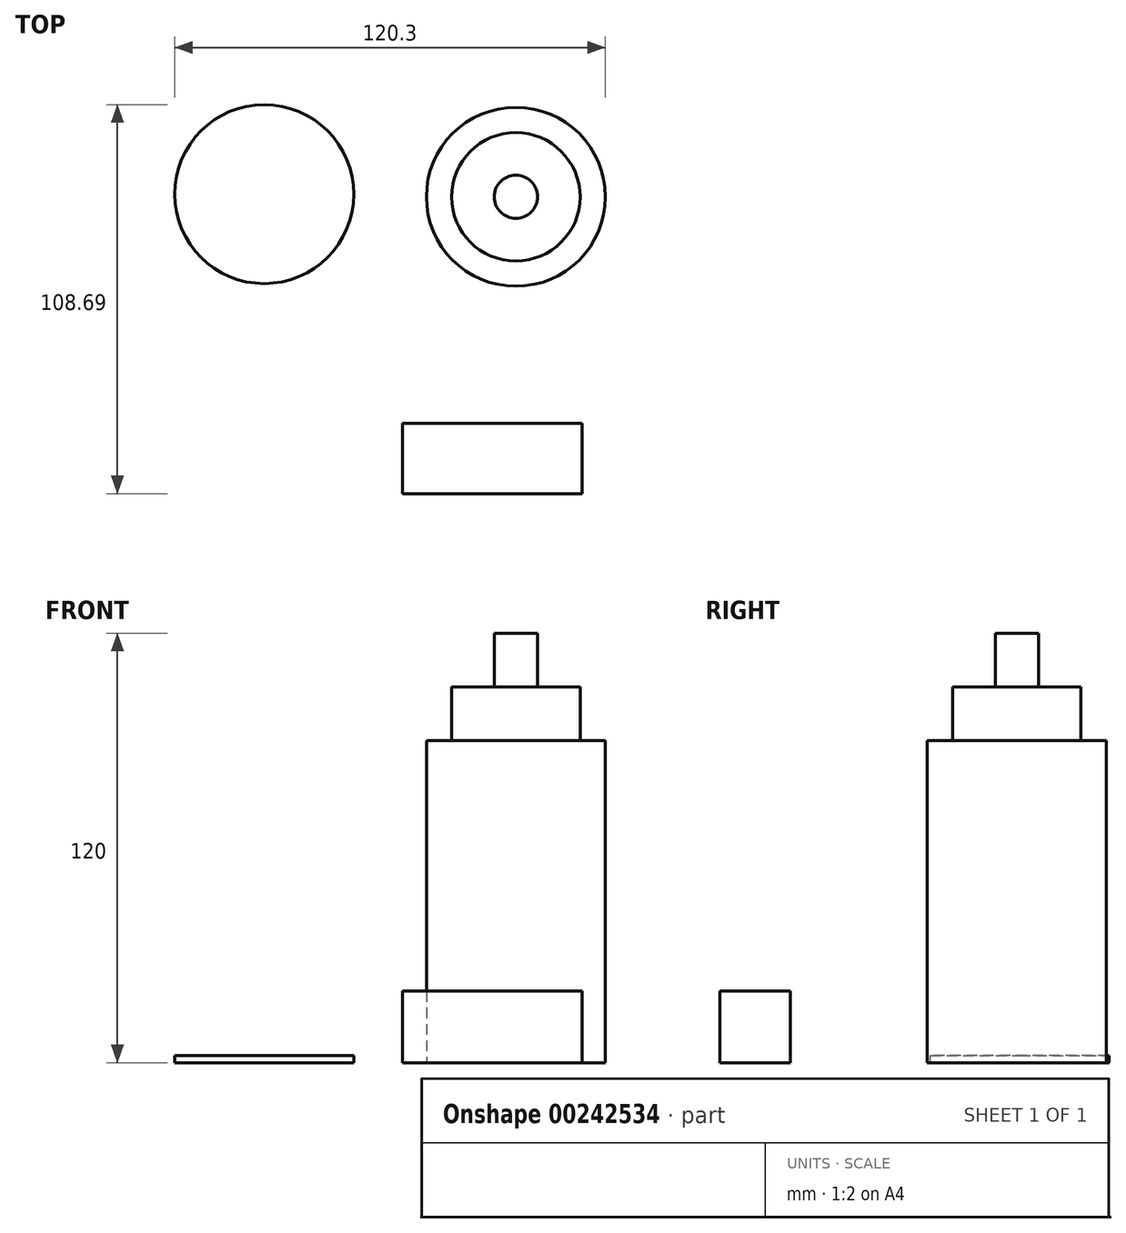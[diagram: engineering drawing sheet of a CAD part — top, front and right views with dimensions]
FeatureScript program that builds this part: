
annotation { "Feature Type Name" : "Feature", "Feature Type Description" : "" }
export const myFeature = defineFeature(function(context is Context, id is Id, definition is map)
    precondition{}
    {
        {
            var Q0;
            Q0=qCreatedBy(makeId("Top.planeOp"),FACE);
            var sketch = newSketch(context, id + "F0", { "sketchPlane" : qUnion([Q0])});
            skCircle(sketch, "E0", {"center": v(-32.04, 34.2) * mm, "radius": 25 * mm});
            skSolve(sketch);
        }
        {
            var Q0;
            Q0=sQuery(id+"F0.wireOp",EDGE,"E0");
            extrude(context, id + "F1", {"bodyType" : ToolBodyType.SURFACE, "surfaceEntities" : qUnion([Q0]), "depth" : 20 * mm});
        }
        {
            var Q0;
            Q0=makeQuery(id+"F0.imprint","IMPRINT",FACE,{"disambiguationData":[TD([[makeQuery(id+"F0.imprint","IMPRINT",EDGE,{"derivedFrom":sQuery(id+"F0.wireOp",EDGE,"E0")}),1.0]])]});
            extrude(context, id + "F2", {"entities" : qUnion([Q0]), "depth" : 2 * mm});
        }
        {
            var Q0;
            Q0=qCreatedBy(makeId("Top.planeOp"),FACE);
            var sketch = newSketch(context, id + "F3", { "sketchPlane" : qUnion([Q0])});
            skCircle(sketch, "E1", {"center": v(38.26, 33.46) * mm, "radius": 25 * mm});
            skCircle(sketch, "E2", {"center": v(38.26, 33.46) * mm, "radius": 17.94 * mm});
            skCircle(sketch, "E3", {"center": v(38.26, 33.46) * mm, "radius": 6.04 * mm});
            skSolve(sketch);
        }
        {
            var Q0;
            Q0=makeQuery(id+"F3.imprint","IMPRINT",FACE,{"disambiguationData":[TD([[makeQuery(id+"F3.imprint","IMPRINT",EDGE,{"derivedFrom":sQuery(id+"F3.wireOp",EDGE,"E1")}),1.0]])]});
            extrude(context, id + "F4", {"entities" : qUnion([Q0]), "depth" : 90 * mm});
        }
        {
            var Q0;
            Q0=makeQuery(id+"F3.imprint","IMPRINT",FACE,{"disambiguationData":[TD([[makeQuery(id+"F3.imprint","IMPRINT",EDGE,{"derivedFrom":sQuery(id+"F3.wireOp",EDGE,"E2")}),1.0]])]});
            extrude(context, id + "F5", {"entities" : qUnion([Q0]), "operationType" : NewBodyOperationType.ADD, "depth" : 105 * mm});
        }
        {
            var Q0;
            Q0=makeQuery(id+"F3.imprint","IMPRINT",FACE,{"disambiguationData":[TD([[makeQuery(id+"F3.imprint","IMPRINT",EDGE,{"derivedFrom":sQuery(id+"F3.wireOp",EDGE,"E3")}),1.0]])]});
            extrude(context, id + "F6", {"entities" : qUnion([Q0]), "operationType" : NewBodyOperationType.ADD, "depth" : 120 * mm});
        }
        {
            var Q0;
            Q0=qCreatedBy(makeId("Top.planeOp"),FACE);
            var sketch = newSketch(context, id + "F7", { "sketchPlane" : qUnion([Q0])});
            skLineSegment(sketch, "E4.bottom", {"start": v(59.56, -26.67) * mm, "end": v(3.96, -26.67) * mm});
            skLineSegment(sketch, "E4.top", {"start": v(59.56, -51.74) * mm, "end": v(3.96, -51.74) * mm});
            skLineSegment(sketch, "E4.left", {"start": v(59.56, -26.67) * mm, "end": v(59.56, -51.74) * mm});
            skLineSegment(sketch, "E4.right", {"start": v(3.96, -26.67) * mm, "end": v(3.96, -51.74) * mm});
            skLineSegment(sketch, "E5.bottom", {"start": v(56.73, -29.87) * mm, "end": v(6.6, -29.87) * mm});
            skLineSegment(sketch, "E5.top", {"start": v(56.73, -49.48) * mm, "end": v(6.6, -49.48) * mm});
            skLineSegment(sketch, "E5.left", {"start": v(56.73, -29.87) * mm, "end": v(56.73, -49.48) * mm});
            skLineSegment(sketch, "E5.right", {"start": v(6.6, -29.87) * mm, "end": v(6.6, -49.48) * mm});
            skSolve(sketch);
        }
        {
            var Q0;
            Q0=makeQuery(id+"F7.imprint","IMPRINT",FACE,{"disambiguationData":[TD([[makeQuery(id+"F7.imprint","IMPRINT",EDGE,{"derivedFrom":sQuery(id+"F7.wireOp",EDGE,"E5.bottom")}),1.0]])]});
            extrude(context, id + "F8", {"entities" : qUnion([Q0]), "depth" : 20 * mm});
        }
    });
